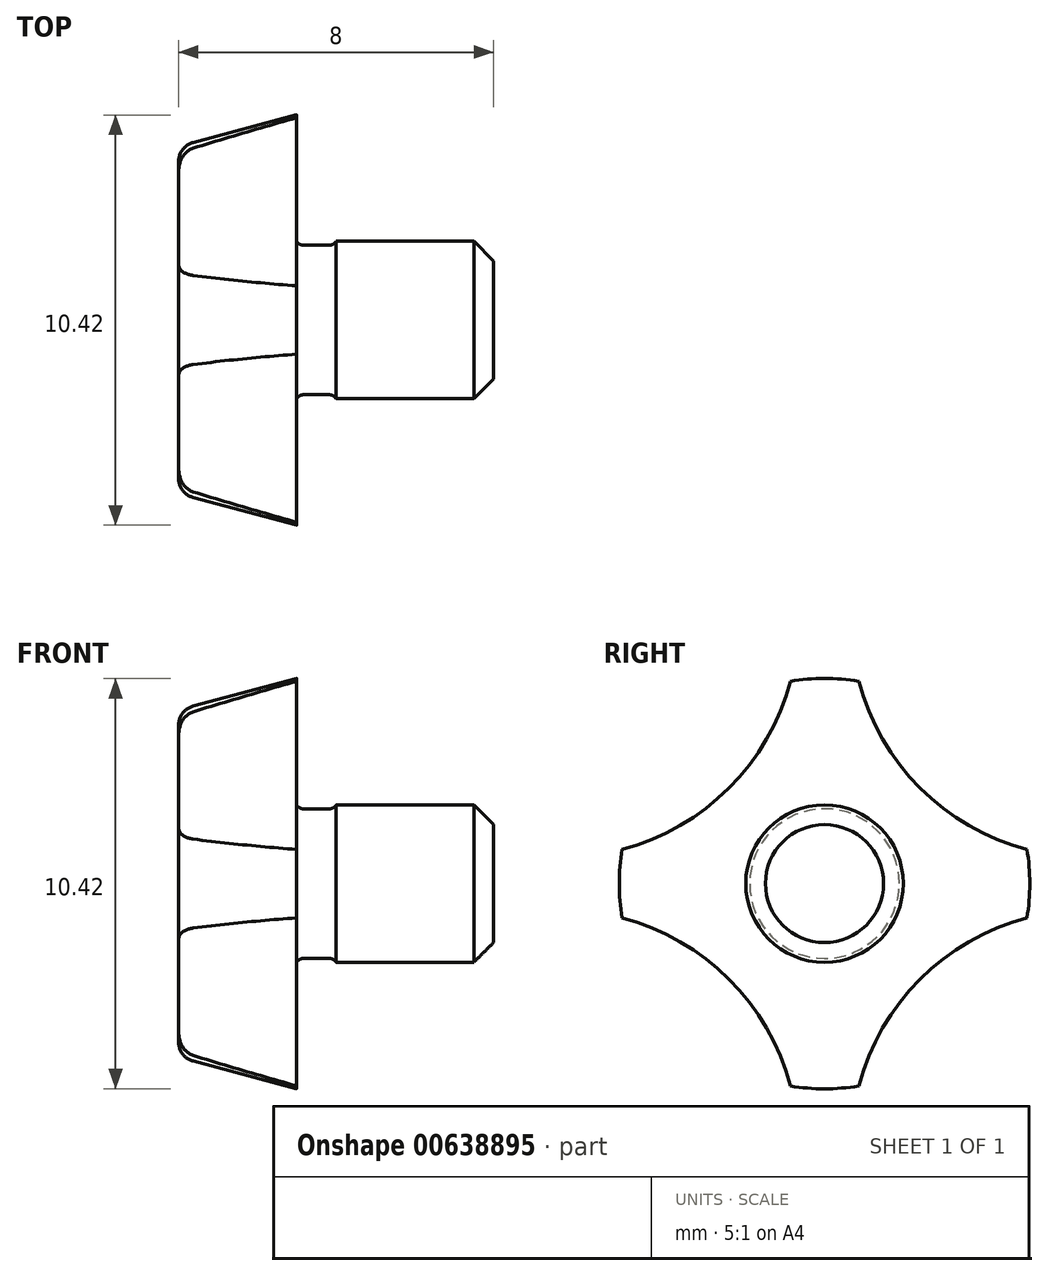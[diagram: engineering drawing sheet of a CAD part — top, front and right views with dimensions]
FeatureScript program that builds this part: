
annotation { "Feature Type Name" : "Feature", "Feature Type Description" : "" }
export const myFeature = defineFeature(function(context is Context, id is Id, definition is map)
    precondition{}
    {
        {
            var Q0;
            Q0=qCreatedBy(makeId("Front.planeOp"),FACE);
            var sketch = newSketch(context, id + "F0", { "sketchPlane" : qUnion([Q0])});
            skLineSegment(sketch, "E0", {"start": v(5.91, 4.03) * mm, "end": v(5.91, -4.03) * mm});
            skLineSegment(sketch, "E1", {"start": v(6.28, -4.5) * mm, "end": v(8.91, -5.21) * mm});
            skLineSegment(sketch, "E2", {"start": v(8.91, -5.21) * mm, "end": v(8.91, 5.21) * mm});
            skArc(sketch, "E3", {"start": v(6.28, 4.5) * mm, "mid": v(6.01, 4.33) * mm, "end": v(5.91, 4.03) * mm});
            skArc(sketch, "E4", {"start": v(5.91, -4.03) * mm, "mid": v(6.01, -4.33) * mm, "end": v(6.28, -4.5) * mm});
            skLineSegment(sketch, "E5", {"start": v(6.28, 4.5) * mm, "end": v(8.91, 5.21) * mm});
            skLineSegment(sketch, "E6", {"start": v(9.08, -1.9) * mm, "end": v(9.08, 1.9) * mm});
            skArc(sketch, "E7", {"start": v(9.08, -1.9) * mm, "mid": v(8.98, -1.93) * mm, "end": v(8.91, -2) * mm});
            skArc(sketch, "E8", {"start": v(8.91, 2) * mm, "mid": v(8.98, 1.93) * mm, "end": v(9.08, 1.9) * mm});
            skLineSegment(sketch, "E9", {"start": v(13.41, -2) * mm, "end": v(13.41, 2) * mm});
            skLineSegment(sketch, "E10", {"start": v(9.91, -2) * mm, "end": v(9.91, 2) * mm});
            skLineSegment(sketch, "E11", {"start": v(9.91, -2) * mm, "end": v(13.41, -2) * mm});
            skLineSegment(sketch, "E12", {"start": v(13.41, 2) * mm, "end": v(9.91, 2) * mm});
            skLineSegment(sketch, "E13", {"start": v(13.91, -1.5) * mm, "end": v(13.91, 1.5) * mm});
            skLineSegment(sketch, "E14", {"start": v(13.41, -2) * mm, "end": v(13.91, -1.5) * mm});
            skLineSegment(sketch, "E15", {"start": v(13.91, 1.5) * mm, "end": v(13.41, 2) * mm});
            skLineSegment(sketch, "E16", {"start": v(9.74, -1.9) * mm, "end": v(9.74, 1.9) * mm});
            skArc(sketch, "E17", {"start": v(9.91, -2) * mm, "mid": v(9.84, -1.93) * mm, "end": v(9.74, -1.9) * mm});
            skArc(sketch, "E18", {"start": v(9.74, 1.9) * mm, "mid": v(9.84, 1.93) * mm, "end": v(9.91, 2) * mm});
            skLineSegment(sketch, "E19", {"start": v(9.08, -1.9) * mm, "end": v(9.74, -1.9) * mm});
            skLineSegment(sketch, "E20", {"start": v(9.74, 1.9) * mm, "end": v(9.08, 1.9) * mm});
            skLineSegment(sketch, "E21", {"start": v(15.27, 0) * mm, "end": v(5.56, 0) * mm});
            skArc(sketch, "E22", {"start": v(-7.83, -5.14) * mm, "mid": v(-5.68, 4.25) * mm, "end": v(-13.84, -0.87) * mm});
            skArc(sketch, "E23", {"start": v(-9.88, -4.25) * mm, "mid": v(-8.7, -4.41) * mm, "end": v(-7.51, -4.25) * mm});
            skArc(sketch, "E24", {"start": v(-13.84, -0.87) * mm, "mid": v(-11.72, -4.25) * mm, "end": v(-7.83, -5.14) * mm});
            skArc(sketch, "E25", {"start": v(-4.45, -1.18) * mm, "mid": v(-4.29, 0) * mm, "end": v(-4.45, 1.18) * mm});
            skArc(sketch, "E26", {"start": v(-3.55, -0.87) * mm, "mid": v(-3.48, 0) * mm, "end": v(-3.55, 0.87) * mm});
            skArc(sketch, "E27", {"start": v(-7.51, 4.25) * mm, "mid": v(-8.7, 4.41) * mm, "end": v(-9.88, 4.25) * mm});
            skArc(sketch, "E28", {"start": v(-7.83, 5.14) * mm, "mid": v(-8.7, 5.21) * mm, "end": v(-9.57, 5.14) * mm});
            skCircle(sketch, "E29", {"center": v(-8.7, 0) * mm, "radius": 2 * mm});
            skArc(sketch, "E30", {"start": v(-12.95, 1.18) * mm, "mid": v(-13.1, 0) * mm, "end": v(-12.95, -1.18) * mm});
            skArc(sketch, "E31", {"start": v(-7.83, 5.14) * mm, "mid": v(-6.27, 2.43) * mm, "end": v(-3.55, 0.87) * mm});
            skArc(sketch, "E32", {"start": v(-13.84, 0.87) * mm, "mid": v(-11.12, 2.43) * mm, "end": v(-9.57, 5.14) * mm});
            skArc(sketch, "E33", {"start": v(-9.57, -5.14) * mm, "mid": v(-11.12, -2.43) * mm, "end": v(-13.84, -0.87) * mm});
            skArc(sketch, "E34", {"start": v(-3.55, -0.87) * mm, "mid": v(-6.27, -2.43) * mm, "end": v(-7.83, -5.14) * mm});
            skPoint(sketch, "E35", {"position": v(13.91, 0) * mm});
            skSolve(sketch);
        }
        {
            var Q0;
            {var subQ0=sQuery(id+"F0.wireOp",EDGE,"E3");Q0=makeQuery(id+"F0.imprint","IMPRINT",FACE,{"disambiguationData":[TD([[makeQuery(id+"F0.imprint","IMPRINT",EDGE,{"derivedFrom":subQ0}),1.0]])]});}
            var Q1;
            {var subQ0=sQuery(id+"F0.wireOp",EDGE,"E18");Q1=makeQuery(id+"F0.imprint","IMPRINT",FACE,{"disambiguationData":[TD([[makeQuery(id+"F0.imprint","IMPRINT",EDGE,{"derivedFrom":subQ0}),-1.0]])]});}
            var Q2;
            {var subQ0=sQuery(id+"F0.wireOp",EDGE,"E12");Q2=makeQuery(id+"F0.imprint","IMPRINT",FACE,{"disambiguationData":[TD([[makeQuery(id+"F0.imprint","IMPRINT",EDGE,{"derivedFrom":subQ0}),1.0]])]});}
            var Q3;
            {var subQ0=sQuery(id+"F0.wireOp",EDGE,"E20");Q3=makeQuery(id+"F0.imprint","IMPRINT",FACE,{"disambiguationData":[TD([[makeQuery(id+"F0.imprint","IMPRINT",EDGE,{"derivedFrom":subQ0}),1.0]])]});}
            var Q4;
            {var subQ0=sQuery(id+"F0.wireOp",EDGE,"E8");Q4=makeQuery(id+"F0.imprint","IMPRINT",FACE,{"disambiguationData":[TD([[makeQuery(id+"F0.imprint","IMPRINT",EDGE,{"derivedFrom":subQ0}),-1.0]])]});}
            var Q5;
            {var subQ0=sQuery(id+"F0.wireOp",EDGE,"E15");Q5=makeQuery(id+"F0.imprint","IMPRINT",FACE,{"disambiguationData":[TD([[makeQuery(id+"F0.imprint","IMPRINT",EDGE,{"derivedFrom":subQ0}),1.0]])]});}
            var Q6;
            Q6=sQuery(id+"F0.wireOp",EDGE,"E21");
            revolve(context, id + "F1", {"entities" : qUnion([Q0, Q1, Q2, Q3, Q4, Q5]), "axis" : qUnion([Q6]), "revolveType" : RevolveType.FULL});
        }
        {
            var Q0;
            Q0=makeQuery(id+"F1.opRevolve","SWEPT_FACE",FACE,{"disambiguationData":[OSD([sQuery(id+"F0.wireOp",EDGE,"E0")])]});
            var sketch = newSketch(context, id + "F2", { "sketchPlane" : qUnion([Q0])});
            skArc(sketch, "E36", {"start": v(0.87, -5.14) * mm, "mid": v(3.02, 4.25) * mm, "end": v(-5.14, -0.87) * mm});
            skArc(sketch, "E37", {"start": v(-1.18, -4.25) * mm, "mid": v(0, -4.41) * mm, "end": v(1.18, -4.25) * mm});
            skArc(sketch, "E38", {"start": v(-5.14, -0.87) * mm, "mid": v(-3.02, -4.25) * mm, "end": v(0.87, -5.14) * mm});
            skArc(sketch, "E39", {"start": v(4.25, -1.18) * mm, "mid": v(4.41, 0) * mm, "end": v(4.25, 1.18) * mm});
            skArc(sketch, "E40", {"start": v(5.14, -0.87) * mm, "mid": v(5.21, 0) * mm, "end": v(5.14, 0.87) * mm});
            skArc(sketch, "E41", {"start": v(1.18, 4.25) * mm, "mid": v(0, 4.41) * mm, "end": v(-1.18, 4.25) * mm});
            skArc(sketch, "E42", {"start": v(0.87, 5.14) * mm, "mid": v(0, 5.21) * mm, "end": v(-0.87, 5.14) * mm});
            skCircle(sketch, "E43", {"center": v(0, 0) * mm, "radius": 2 * mm});
            skArc(sketch, "E44", {"start": v(-4.25, 1.18) * mm, "mid": v(-4.41, 0) * mm, "end": v(-4.25, -1.18) * mm});
            skArc(sketch, "E45", {"start": v(0.87, 5.14) * mm, "mid": v(2.43, 2.43) * mm, "end": v(5.14, 0.87) * mm});
            skArc(sketch, "E46", {"start": v(-5.14, 0.87) * mm, "mid": v(-2.43, 2.43) * mm, "end": v(-0.87, 5.14) * mm});
            skArc(sketch, "E47", {"start": v(-0.87, -5.14) * mm, "mid": v(-2.43, -2.43) * mm, "end": v(-5.14, -0.87) * mm});
            skArc(sketch, "E48", {"start": v(5.14, -0.87) * mm, "mid": v(2.43, -2.43) * mm, "end": v(0.87, -5.14) * mm});
            skSolve(sketch);
        }
        {
            var Q0;
            {var subQ0=sQuery(id+"F2.wireOp",EDGE,"E46");var subQ1=makeQuery(id+"F1.opRevolve","SWEPT_EDGE",EDGE,{"disambiguationData":[OSD([sQuery(id+"F0.wireOp",EDGE,"E0"),sQuery(id+"F0.wireOp",EDGE,"E3")])]});var subQ2=makeQuery(id+"F2.imprint","INTERSECT",VERTEX,{"disambiguationData":[OD(0.0)],"derivedFrom":[subQ1,subQ0]});Q0=makeQuery(id+"F2.imprint","IMPRINT",FACE,{"disambiguationData":[TD([[makeQuery(id+"F2.imprint","IMPRINT",EDGE,{"disambiguationData":[TD([[subQ2,-1.0]])],"derivedFrom":subQ0}),1.0]])]});}
            var Q1;
            {var subQ0=sQuery(id+"F2.wireOp",EDGE,"E46");var subQ4=makeQuery(id+"F2.imprint","INTERSECT",VERTEX,{"derivedFrom":[sQuery(id+"F2.wireOp",EDGE,"E44"),subQ0]});Q1=makeQuery(id+"F2.imprint","IMPRINT",FACE,{"disambiguationData":[TD([[makeQuery(id+"F2.imprint","IMPRINT",EDGE,{"disambiguationData":[TD([[subQ4,1.0]])],"derivedFrom":subQ0}),1.0]])]});}
            var Q2;
            {var subQ0=sQuery(id+"F2.wireOp",EDGE,"E47");var subQ1=makeQuery(id+"F1.opRevolve","SWEPT_EDGE",EDGE,{"disambiguationData":[OSD([sQuery(id+"F0.wireOp",EDGE,"E0"),sQuery(id+"F0.wireOp",EDGE,"E3")])]});var subQ2=makeQuery(id+"F2.imprint","INTERSECT",VERTEX,{"disambiguationData":[OD(0.0)],"derivedFrom":[subQ1,subQ0]});Q2=makeQuery(id+"F2.imprint","IMPRINT",FACE,{"disambiguationData":[TD([[makeQuery(id+"F2.imprint","IMPRINT",EDGE,{"disambiguationData":[TD([[subQ2,-1.0]])],"derivedFrom":subQ0}),1.0]])]});}
            var Q3;
            {var subQ0=sQuery(id+"F2.wireOp",EDGE,"E47");var subQ4=makeQuery(id+"F2.imprint","INTERSECT",VERTEX,{"derivedFrom":[sQuery(id+"F2.wireOp",EDGE,"E37"),subQ0]});Q3=makeQuery(id+"F2.imprint","IMPRINT",FACE,{"disambiguationData":[TD([[makeQuery(id+"F2.imprint","IMPRINT",EDGE,{"disambiguationData":[TD([[subQ4,1.0]])],"derivedFrom":subQ0}),1.0]])]});}
            var Q4;
            {var subQ0=sQuery(id+"F2.wireOp",EDGE,"E48");var subQ4=makeQuery(id+"F2.imprint","INTERSECT",VERTEX,{"derivedFrom":[sQuery(id+"F2.wireOp",EDGE,"E39"),subQ0]});Q4=makeQuery(id+"F2.imprint","IMPRINT",FACE,{"disambiguationData":[TD([[makeQuery(id+"F2.imprint","IMPRINT",EDGE,{"disambiguationData":[TD([[subQ4,1.0]])],"derivedFrom":subQ0}),1.0]])]});}
            var Q5;
            {var subQ0=sQuery(id+"F2.wireOp",EDGE,"E48");var subQ1=makeQuery(id+"F1.opRevolve","SWEPT_EDGE",EDGE,{"disambiguationData":[OSD([sQuery(id+"F0.wireOp",EDGE,"E0"),sQuery(id+"F0.wireOp",EDGE,"E3")])]});var subQ2=makeQuery(id+"F2.imprint","INTERSECT",VERTEX,{"disambiguationData":[OD(0.0)],"derivedFrom":[subQ1,subQ0]});Q5=makeQuery(id+"F2.imprint","IMPRINT",FACE,{"disambiguationData":[TD([[makeQuery(id+"F2.imprint","IMPRINT",EDGE,{"disambiguationData":[TD([[subQ2,-1.0]])],"derivedFrom":subQ0}),1.0]])]});}
            var Q6;
            {var subQ0=sQuery(id+"F2.wireOp",EDGE,"E45");var subQ1=makeQuery(id+"F1.opRevolve","SWEPT_EDGE",EDGE,{"disambiguationData":[OSD([sQuery(id+"F0.wireOp",EDGE,"E0"),sQuery(id+"F0.wireOp",EDGE,"E3")])]});var subQ2=makeQuery(id+"F2.imprint","INTERSECT",VERTEX,{"disambiguationData":[OD(0.0)],"derivedFrom":[subQ1,subQ0]});Q6=makeQuery(id+"F2.imprint","IMPRINT",FACE,{"disambiguationData":[TD([[makeQuery(id+"F2.imprint","IMPRINT",EDGE,{"disambiguationData":[TD([[subQ2,-1.0]])],"derivedFrom":subQ0}),1.0]])]});}
            var Q7;
            {var subQ0=sQuery(id+"F2.wireOp",EDGE,"E45");var subQ1=makeQuery(id+"F2.imprint","INTERSECT",VERTEX,{"derivedFrom":[sQuery(id+"F2.wireOp",EDGE,"E41"),subQ0]});Q7=makeQuery(id+"F2.imprint","IMPRINT",FACE,{"disambiguationData":[TD([[makeQuery(id+"F2.imprint","IMPRINT",EDGE,{"disambiguationData":[TD([[subQ1,1.0]])],"derivedFrom":subQ0}),1.0]])]});}
            extrude(context, id + "F3", {"entities" : qUnion([Q0, Q1, Q2, Q3, Q4, Q5, Q6, Q7]), "operationType" : NewBodyOperationType.REMOVE, "oppositeDirection" : true, "depth" : 25 * mm, "offsetDistance" : 25 * mm});
        }
    });
